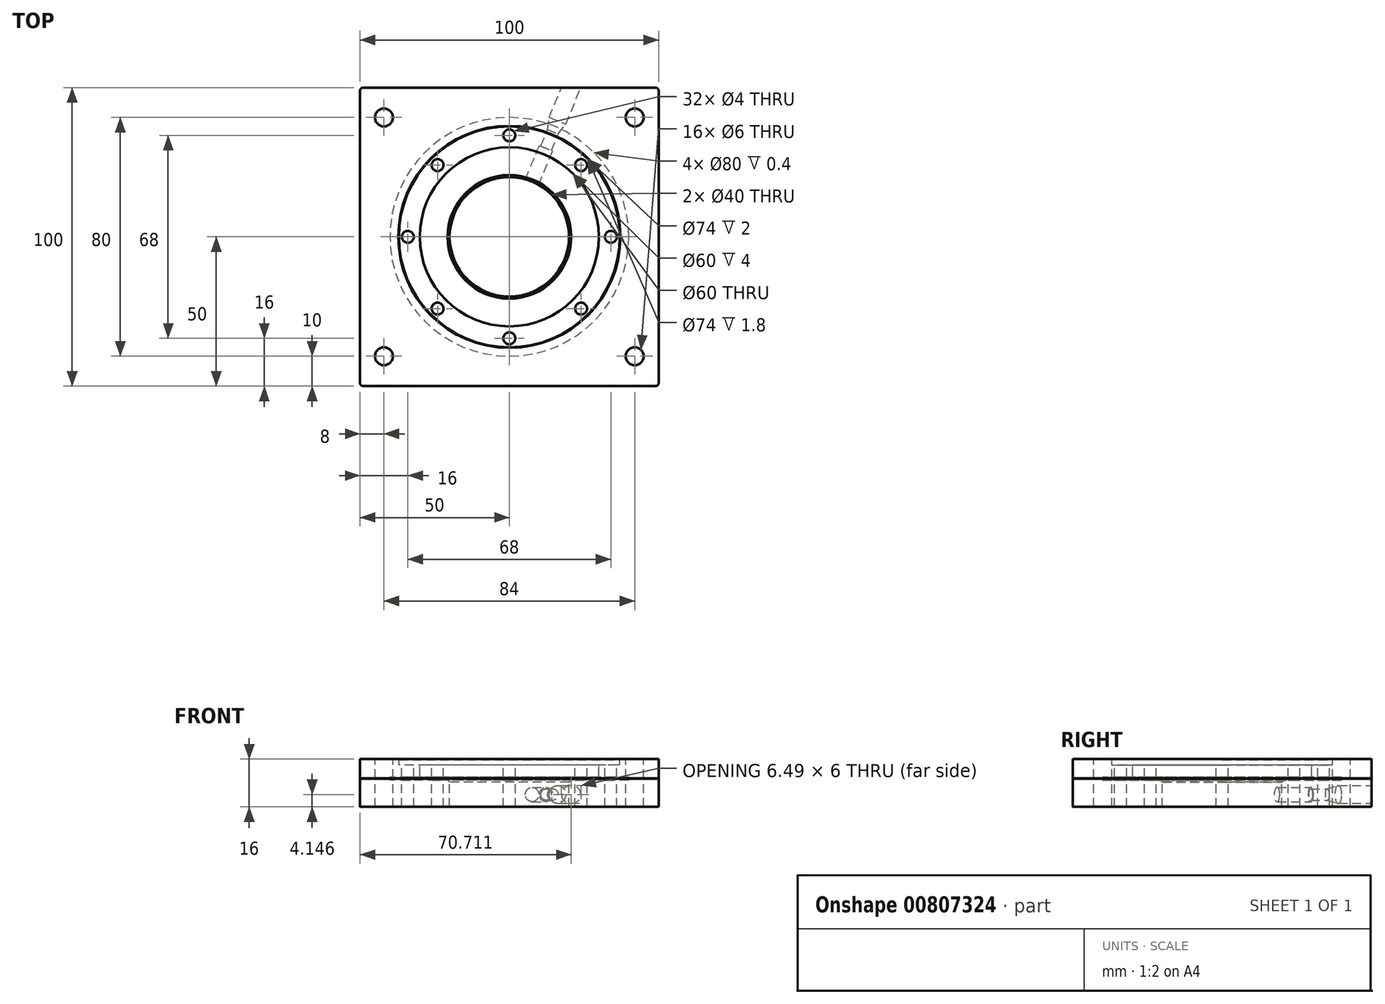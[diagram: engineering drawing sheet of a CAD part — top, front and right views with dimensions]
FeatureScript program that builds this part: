
annotation { "Feature Type Name" : "Feature", "Feature Type Description" : "" }
export const myFeature = defineFeature(function(context is Context, id is Id, definition is map)
    precondition{}
    {
        {
            var Q0;
            Q0=qCreatedBy(makeId("Front.planeOp"),FACE);
            var sketch = newSketch(context, id + "F0", { "sketchPlane" : qUnion([Q0])});
            skLineSegment(sketch, "E0", {"start": v(0, 61.42) * mm, "end": v(0, -61.42) * mm, "construction": true});
            skLineSegment(sketch, "E1", {"start": v(-106.58, 0) * mm, "end": v(106.58, 0) * mm, "construction": true});
            skPoint(sketch, "E2", {"position": v(0, 0) * mm});
            skLineSegment(sketch, "E3.bottom", {"start": v(-75, 8) * mm, "end": v(75, 8) * mm});
            skLineSegment(sketch, "E3.top", {"start": v(-75, -8) * mm, "end": v(75, -8) * mm});
            skLineSegment(sketch, "E3.left", {"start": v(-75, 8) * mm, "end": v(-75, -8) * mm});
            skLineSegment(sketch, "E3.right", {"start": v(75, 8) * mm, "end": v(75, -8) * mm});
            skLineSegment(sketch, "E4", {"start": v(-40, 2) * mm, "end": v(-40, 1) * mm});
            skLineSegment(sketch, "E5.MirrorCS", {"start": v(40, 2) * mm, "end": v(40, 1) * mm});
            skLineSegment(sketch, "E6", {"start": v(-37, 8) * mm, "end": v(-37, 6) * mm});
            skLineSegment(sketch, "E7", {"start": v(-20, 1) * mm, "end": v(-20, -8) * mm});
            skLineSegment(sketch, "E8.MirrorCS", {"start": v(20, 1) * mm, "end": v(20, -8) * mm});
            skLineSegment(sketch, "E9.MirrorCS", {"start": v(37, 8) * mm, "end": v(37, 6) * mm});
            skLineSegment(sketch, "E10", {"start": v(30, 6) * mm, "end": v(37, 6) * mm});
            skLineSegment(sketch, "E11", {"start": v(-40, 1) * mm, "end": v(40, 1) * mm});
            skLineSegment(sketch, "E12", {"start": v(-40, 1.6) * mm, "end": v(-75, 1.6) * mm});
            skLineSegment(sketch, "E13", {"start": v(-75, 1.4) * mm, "end": v(-40, 1.4) * mm});
            skLineSegment(sketch, "E14.MirrorCS", {"start": v(40, 1.6) * mm, "end": v(75, 1.6) * mm});
            skLineSegment(sketch, "E15.MirrorCS", {"start": v(75, 1.4) * mm, "end": v(40, 1.4) * mm});
            skLineSegment(sketch, "E16", {"start": v(-20, 0.3) * mm, "end": v(-20.7, 1) * mm});
            skLineSegment(sketch, "E17.MirrorCS", {"start": v(20, 0.3) * mm, "end": v(20.7, 1) * mm});
            skLineSegment(sketch, "E18", {"start": v(-20, 0.3) * mm, "end": v(20, 0.3) * mm});
            skPoint(sketch, "E19.newPointA", {"position": v(30, 6) * mm});
            skLineSegment(sketch, "E20", {"start": v(-30, 6) * mm, "end": v(-37, 6) * mm});
            skPoint(sketch, "E21.visualSharp", {"position": v(-30, 6) * mm});
            skLineSegment(sketch, "E22", {"start": v(-40, 2) * mm, "end": v(40, 2) * mm});
            skLineSegment(sketch, "E23", {"start": v(30, 6) * mm, "end": v(30, 2) * mm});
            skLineSegment(sketch, "E24", {"start": v(-30, 6) * mm, "end": v(-30, 2) * mm});
            skSolve(sketch);
        }
        {
            var Q0;
            {var subQ0=sQuery(id+"F0.wireOp",EDGE,"E6");Q0=makeQuery(id+"F0.imprint","IMPRINT",FACE,{"disambiguationData":[TD([[makeQuery(id+"F0.imprint","IMPRINT",EDGE,{"derivedFrom":subQ0}),-1.0]])]});}
            var Q1;
            {var subQ4=sQuery(id+"F0.wireOp",EDGE,"E13");Q1=makeQuery(id+"F0.imprint","IMPRINT",FACE,{"disambiguationData":[TD([[makeQuery(id+"F0.imprint","IMPRINT",EDGE,{"derivedFrom":subQ4}),-1.0]])]});}
            var Q2;
            {var subQ6=sQuery(id+"F0.wireOp",EDGE,"E15.MirrorCS");Q2=makeQuery(id+"F0.imprint","IMPRINT",FACE,{"disambiguationData":[TD([[makeQuery(id+"F0.imprint","IMPRINT",EDGE,{"derivedFrom":subQ6}),1.0]])]});}
            var Q3;
            {var subQ0=sQuery(id+"F0.wireOp",EDGE,"E9.MirrorCS");Q3=makeQuery(id+"F0.imprint","IMPRINT",FACE,{"disambiguationData":[TD([[makeQuery(id+"F0.imprint","IMPRINT",EDGE,{"derivedFrom":subQ0}),1.0]])]});}
            var Q4;
            Q4=sQuery(id+"F0.wireOp",EDGE,"E0");
            revolve(context, id + "F1", {"entities" : qUnion([Q0, Q1, Q2, Q3]), "axis" : qUnion([Q4]), "revolveType" : RevolveType.FULL});
        }
        {
            var Q0;
            {var subQ0=sQuery(id+"F0.wireOp",EDGE,"E3.bottom");Q0=makeQuery(id+"F1.opRevolve","SWEPT_FACE",FACE,{"disambiguationData":[OSD([subQ0]),TDD([makeQuery(id+"F0.imprint","IMPRINT",EDGE,{"disambiguationData":[TD([[makeQuery(id+"F0.imprint","INTERSECT",VERTEX,{"derivedFrom":[subQ0,sQuery(id+"F0.wireOp",EDGE,"E3.left")]}),-1.0]])],"derivedFrom":subQ0})])]});}
            var sketch = newSketch(context, id + "F2", { "sketchPlane" : qUnion([Q0])});
            skLineSegment(sketch, "E25.bottom", {"start": v(-50, 50) * mm, "end": v(50, 50) * mm});
            skLineSegment(sketch, "E25.top", {"start": v(-50, -50) * mm, "end": v(50, -50) * mm});
            skLineSegment(sketch, "E25.left", {"start": v(-50, 50) * mm, "end": v(-50, -50) * mm});
            skLineSegment(sketch, "E25.right", {"start": v(50, 50) * mm, "end": v(50, -50) * mm});
            skPoint(sketch, "E25.middle", {"position": v(0, 0) * mm});
            skLineSegment(sketch, "E26.bottom", {"start": v(-85, 85) * mm, "end": v(85, 85) * mm});
            skLineSegment(sketch, "E26.top", {"start": v(-85, -85) * mm, "end": v(85, -85) * mm});
            skLineSegment(sketch, "E26.left", {"start": v(-85, 85) * mm, "end": v(-85, -85) * mm});
            skLineSegment(sketch, "E26.right", {"start": v(85, 85) * mm, "end": v(85, -85) * mm});
            skSolve(sketch);
        }
        {
            var Q0;
            Q0=makeQuery(id+"F2.imprint","IMPRINT",FACE,{"disambiguationData":[TD([[makeQuery(id+"F2.imprint","IMPRINT",EDGE,{"derivedFrom":sQuery(id+"F2.wireOp",EDGE,"E26.bottom")}),-1.0]])]});
            var Q1;
            Q1=makeQuery(id+"F2.imprint","IMPRINT",FACE,{"disambiguationData":[TD([[makeQuery(id+"F2.imprint","IMPRINT",EDGE,{"derivedFrom":sQuery(id+"F2.wireOp",EDGE,"E25.bottom")}),1.0]])]});
            extrude(context, id + "F3", {"entities" : qUnion([Q0, Q1]), "operationType" : NewBodyOperationType.REMOVE, "endBound" : BoundingType.THROUGH_ALL, "oppositeDirection" : true, "depth" : 25 * mm, "offsetDistance" : 25 * mm});
        }
        {
            var Q0;
            {var subQ0=sQuery(id+"F0.wireOp",EDGE,"E3.bottom");Q0=makeQuery(id+"F1.opRevolve","SWEPT_FACE",FACE,{"disambiguationData":[OSD([subQ0]),TDD([makeQuery(id+"F0.imprint","IMPRINT",EDGE,{"disambiguationData":[TD([[makeQuery(id+"F0.imprint","INTERSECT",VERTEX,{"derivedFrom":[subQ0,sQuery(id+"F0.wireOp",EDGE,"E3.right")]}),1.0]])],"derivedFrom":subQ0})])]});}
            var sketch = newSketch(context, id + "F4", { "sketchPlane" : qUnion([Q0])});
            skLineSegment(sketch, "E27.0.0", {"start": v(-50, 50) * mm, "end": v(-50, -50) * mm});
            skLineSegment(sketch, "E27.0.1", {"start": v(-50, -50) * mm, "end": v(50, -50) * mm});
            skLineSegment(sketch, "E27.0.2", {"start": v(50, -50) * mm, "end": v(50, 50) * mm});
            skLineSegment(sketch, "E27.0.3", {"start": v(50, 50) * mm, "end": v(-50, 50) * mm});
            skCircle(sketch, "E28.0.0", {"center": v(0, 0) * mm, "radius": 37 * mm});
            skCircle(sketch, "E29.0", {"center": v(0, 0) * mm, "radius": 20 * mm});
            skCircle(sketch, "E30.0", {"center": v(0, 0) * mm, "radius": 20.7 * mm});
            skLineSegment(sketch, "E31", {"start": v(-50, 0) * mm, "end": v(50, 0) * mm, "construction": true});
            skLineSegment(sketch, "E32", {"start": v(0, 50) * mm, "end": v(0, -50) * mm, "construction": true});
            skLineSegment(sketch, "E33", {"start": v(-50, 40) * mm, "end": v(50, 40) * mm, "construction": true});
            skLineSegment(sketch, "E34", {"start": v(42, 50) * mm, "end": v(42, -50) * mm, "construction": true});
            skCircle(sketch, "E35", {"center": v(42, 40) * mm, "radius": 3 * mm});
            skCircle(sketch, "E36.0.1.0", {"center": v(42, -40) * mm, "radius": 3 * mm});
            skCircle(sketch, "E36.1.0.0", {"center": v(-42, 40) * mm, "radius": 3 * mm});
            skCircle(sketch, "E36.1.1.0", {"center": v(-42, -40) * mm, "radius": 3 * mm});
            skLineSegment(sketch, "E36.direction1", {"start": v(42, 40) * mm, "end": v(-42, 40) * mm, "construction": true});
            skLineSegment(sketch, "E36.direction2", {"start": v(42, 40) * mm, "end": v(42, -40) * mm, "construction": true});
            skCircle(sketch, "E37", {"center": v(0, 0) * mm, "radius": 34 * mm, "construction": true});
            skCircle(sketch, "E38.0", {"center": v(0, 0) * mm, "radius": 30 * mm});
            skCircle(sketch, "E39", {"center": v(0, 34) * mm, "radius": 2 * mm});
            skCircle(sketch, "E40.1.0", {"center": v(-24.04, 24.04) * mm, "radius": 2 * mm});
            skCircle(sketch, "E40.2.0", {"center": v(-34, 0) * mm, "radius": 2 * mm});
            skCircle(sketch, "E40.3.0", {"center": v(-24.04, -24.04) * mm, "radius": 2 * mm});
            skCircle(sketch, "E40.4.0", {"center": v(0, -34) * mm, "radius": 2 * mm});
            skCircle(sketch, "E40.5.0", {"center": v(24.04, -24.04) * mm, "radius": 2 * mm});
            skCircle(sketch, "E40.6.0", {"center": v(34, 0) * mm, "radius": 2 * mm});
            skCircle(sketch, "E40.7.0", {"center": v(24.04, 24.04) * mm, "radius": 2 * mm});
            skLineSegment(sketch, "E41", {"start": v(0, 0) * mm, "end": v(20.71, 50) * mm, "construction": true});
            skSolve(sketch);
        }
        {
            var Q0;
            Q0=makeQuery(id+"F4.imprint","IMPRINT",FACE,{"disambiguationData":[TD([[makeQuery(id+"F4.imprint","IMPRINT",EDGE,{"derivedFrom":sQuery(id+"F4.wireOp",EDGE,"E36.1.0.0")}),1.0]])]});
            var Q1;
            Q1=makeQuery(id+"F4.imprint","IMPRINT",FACE,{"disambiguationData":[TD([[makeQuery(id+"F4.imprint","IMPRINT",EDGE,{"derivedFrom":sQuery(id+"F4.wireOp",EDGE,"E35")}),1.0]])]});
            var Q2;
            Q2=makeQuery(id+"F4.imprint","IMPRINT",FACE,{"disambiguationData":[TD([[makeQuery(id+"F4.imprint","IMPRINT",EDGE,{"derivedFrom":sQuery(id+"F4.wireOp",EDGE,"E36.0.1.0")}),1.0]])]});
            var Q3;
            Q3=makeQuery(id+"F4.imprint","IMPRINT",FACE,{"disambiguationData":[TD([[makeQuery(id+"F4.imprint","IMPRINT",EDGE,{"derivedFrom":sQuery(id+"F4.wireOp",EDGE,"E36.1.1.0")}),1.0]])]});
            extrude(context, id + "F5", {"entities" : qUnion([Q0, Q1, Q2, Q3]), "operationType" : NewBodyOperationType.REMOVE, "endBound" : BoundingType.THROUGH_ALL, "oppositeDirection" : true, "depth" : 25 * mm, "offsetDistance" : 25 * mm});
        }
        {
            var Q0;
            Q0=makeQuery(id+"F4.imprint","IMPRINT",FACE,{"disambiguationData":[TD([[makeQuery(id+"F4.imprint","IMPRINT",EDGE,{"derivedFrom":sQuery(id+"F4.wireOp",EDGE,"E40.1.0")}),1.0]])]});
            var Q1;
            Q1=makeQuery(id+"F4.imprint","IMPRINT",FACE,{"disambiguationData":[TD([[makeQuery(id+"F4.imprint","IMPRINT",EDGE,{"derivedFrom":sQuery(id+"F4.wireOp",EDGE,"E39")}),1.0]])]});
            var Q2;
            Q2=makeQuery(id+"F4.imprint","IMPRINT",FACE,{"disambiguationData":[TD([[makeQuery(id+"F4.imprint","IMPRINT",EDGE,{"derivedFrom":sQuery(id+"F4.wireOp",EDGE,"E40.7.0")}),1.0]])]});
            var Q3;
            Q3=makeQuery(id+"F4.imprint","IMPRINT",FACE,{"disambiguationData":[TD([[makeQuery(id+"F4.imprint","IMPRINT",EDGE,{"derivedFrom":sQuery(id+"F4.wireOp",EDGE,"E40.6.0")}),1.0]])]});
            var Q4;
            Q4=makeQuery(id+"F4.imprint","IMPRINT",FACE,{"disambiguationData":[TD([[makeQuery(id+"F4.imprint","IMPRINT",EDGE,{"derivedFrom":sQuery(id+"F4.wireOp",EDGE,"E40.5.0")}),1.0]])]});
            var Q5;
            Q5=makeQuery(id+"F4.imprint","IMPRINT",FACE,{"disambiguationData":[TD([[makeQuery(id+"F4.imprint","IMPRINT",EDGE,{"derivedFrom":sQuery(id+"F4.wireOp",EDGE,"E40.4.0")}),1.0]])]});
            var Q6;
            Q6=makeQuery(id+"F4.imprint","IMPRINT",FACE,{"disambiguationData":[TD([[makeQuery(id+"F4.imprint","IMPRINT",EDGE,{"derivedFrom":sQuery(id+"F4.wireOp",EDGE,"E40.3.0")}),1.0]])]});
            var Q7;
            Q7=makeQuery(id+"F4.imprint","IMPRINT",FACE,{"disambiguationData":[TD([[makeQuery(id+"F4.imprint","IMPRINT",EDGE,{"derivedFrom":sQuery(id+"F4.wireOp",EDGE,"E40.2.0")}),1.0]])]});
            extrude(context, id + "F6", {"entities" : qUnion([Q0, Q1, Q2, Q3, Q4, Q5, Q6, Q7]), "operationType" : NewBodyOperationType.REMOVE, "endBound" : BoundingType.THROUGH_ALL, "oppositeDirection" : true, "depth" : 25 * mm, "offsetDistance" : 25 * mm});
        }
        {
            var Q0;
            {var subQ0=sQuery(id+"F0.wireOp",EDGE,"E3.top");Q0=makeQuery(id+"F1.opRevolve","SWEPT_FACE",FACE,{"disambiguationData":[OSD([subQ0]),TDD([makeQuery(id+"F0.imprint","IMPRINT",EDGE,{"disambiguationData":[TD([[makeQuery(id+"F0.imprint","INTERSECT",VERTEX,{"derivedFrom":[subQ0,sQuery(id+"F0.wireOp",EDGE,"E3.right")]}),1.0]])],"derivedFrom":subQ0})])]});}
            var sketch = newSketch(context, id + "F7", { "sketchPlane" : qUnion([Q0])});
            skLineSegment(sketch, "E42.0", {"start": v(-50, -50) * mm, "end": v(50, -50) * mm});
            skCircle(sketch, "E43.0", {"center": v(0, 0) * mm, "radius": 20 * mm, "construction": true});
            skLineSegment(sketch, "E44.0.0", {"start": v(50, 50) * mm, "end": v(-50, 50) * mm});
            skLineSegment(sketch, "E44.0.1", {"start": v(-50, 50) * mm, "end": v(-50, -50) * mm});
            skLineSegment(sketch, "E44.0.3", {"start": v(50, -50) * mm, "end": v(50, 50) * mm});
            skLineSegment(sketch, "E45.0", {"start": v(0, 0) * mm, "end": v(20.71, -50) * mm, "construction": true});
            skLineSegment(sketch, "E46.0", {"start": v(0, -50) * mm, "end": v(0, 50) * mm, "construction": true});
            skLineSegment(sketch, "E47.0", {"start": v(-50, 0) * mm, "end": v(50, 0) * mm, "construction": true});
            skSolve(sketch);
        }
        {
            var Q0;
            Q0=makeQuery(id+"F7.imprint","IMPRINT",FACE,{"disambiguationData":[TD([[makeQuery(id+"F7.imprint","IMPRINT",EDGE,{"derivedFrom":sQuery(id+"F7.wireOp",EDGE,"E44.0.0")}),-1.0]])]});
            cPlane(context, id + "F8", {"entities" : qUnion([Q0]), "cplaneType" : CPlaneType.OFFSET, "offset" : 4.15 * mm, "oppositeDirection" : true, "width" : 150 * mm, "height" : 150 * mm});
        }
        {
            var Q0;
            Q0=qCreatedBy(id+"F8.planeOp",FACE);
            var sketch = newSketch(context, id + "F9", { "sketchPlane" : qUnion([Q0])});
            skLineSegment(sketch, "E48.0", {"start": v(-50, -50) * mm, "end": v(50, -50) * mm});
            skLineSegment(sketch, "E49.0", {"start": v(50, -50) * mm, "end": v(50, 50) * mm});
            skLineSegment(sketch, "E50.0", {"start": v(-50, 50) * mm, "end": v(-50, -50) * mm});
            skLineSegment(sketch, "E51.0", {"start": v(50, 50) * mm, "end": v(-50, 50) * mm});
            skCircle(sketch, "E52.0", {"center": v(0, 0) * mm, "radius": 20 * mm, "construction": true});
            skLineSegment(sketch, "E53.0", {"start": v(0, -50) * mm, "end": v(0, 50) * mm, "construction": true});
            skLineSegment(sketch, "E54.0", {"start": v(-50, 0) * mm, "end": v(50, 0) * mm, "construction": true});
            skLineSegment(sketch, "E55.0", {"start": v(0, 0) * mm, "end": v(20.71, -50) * mm});
            skLineSegment(sketch, "E56", {"start": v(23.48, -48.85) * mm, "end": v(17.94, -51.15) * mm});
            skLineSegment(sketch, "E57", {"start": v(18.9, -37.77) * mm, "end": v(13.35, -40.06) * mm});
            skLineSegment(sketch, "E58", {"start": v(16.34, -34.5) * mm, "end": v(12.83, -35.95) * mm});
            skLineSegment(sketch, "E59", {"start": v(14.5, -28.76) * mm, "end": v(10.07, -30.6) * mm});
            skPoint(sketch, "E60", {"position": v(12.3, -29.67) * mm});
            skPoint(sketch, "E61", {"position": v(14.59, -35.22) * mm});
            skPoint(sketch, "E62", {"position": v(16.12, -38.91) * mm});
            skLineSegment(sketch, "E63", {"start": v(23.48, -48.85) * mm, "end": v(18.9, -37.77) * mm});
            skLineSegment(sketch, "E64", {"start": v(17.94, -51.15) * mm, "end": v(13.35, -40.06) * mm});
            skLineSegment(sketch, "E65", {"start": v(18.9, -37.77) * mm, "end": v(16.34, -34.5) * mm});
            skLineSegment(sketch, "E66", {"start": v(13.35, -40.06) * mm, "end": v(12.83, -35.95) * mm});
            skLineSegment(sketch, "E67", {"start": v(9.15, -15.82) * mm, "end": v(4.72, -17.66) * mm});
            skPoint(sketch, "E68", {"position": v(6.93, -16.74) * mm});
            skLineSegment(sketch, "E69", {"start": v(14.5, -28.76) * mm, "end": v(9.15, -15.82) * mm});
            skLineSegment(sketch, "E70", {"start": v(10.07, -30.6) * mm, "end": v(4.72, -17.66) * mm});
            skLineSegment(sketch, "E71", {"start": v(14.05, -28.95) * mm, "end": v(10.54, -30.4) * mm});
            skLineSegment(sketch, "E72", {"start": v(16.34, -34.5) * mm, "end": v(14.05, -28.95) * mm});
            skLineSegment(sketch, "E73", {"start": v(12.83, -35.95) * mm, "end": v(10.54, -30.4) * mm});
            skLineSegment(sketch, "E74", {"start": v(23.48, -48.85) * mm, "end": v(24.63, -51.62) * mm});
            skLineSegment(sketch, "E75", {"start": v(24.63, -51.62) * mm, "end": v(19.09, -53.92) * mm});
            skLineSegment(sketch, "E76", {"start": v(19.09, -53.92) * mm, "end": v(17.94, -51.15) * mm});
            skPoint(sketch, "E77", {"position": v(21.86, -52.77) * mm});
            skLineSegment(sketch, "E78", {"start": v(20.71, -50) * mm, "end": v(21.86, -52.77) * mm});
            skSolve(sketch);
        }
        {
            var Q0;
            {var subQ2=sQuery(id+"F9.wireOp",EDGE,"E76");Q0=makeQuery(id+"F9.imprint","IMPRINT",FACE,{"disambiguationData":[TD([[makeQuery(id+"F9.imprint","IMPRINT",EDGE,{"derivedFrom":subQ2}),-1.0]])]});}
            var Q1;
            {var subQ1=sQuery(id+"F9.wireOp",EDGE,"E48.0");var subQ3=sQuery(id+"F9.wireOp",EDGE,"E64");var subQ4=makeQuery(id+"F9.imprint","INTERSECT",VERTEX,{"derivedFrom":[subQ1,subQ3]});Q1=makeQuery(id+"F9.imprint","IMPRINT",FACE,{"disambiguationData":[TD([[makeQuery(id+"F9.imprint","IMPRINT",EDGE,{"disambiguationData":[TD([[subQ4,1.0]])],"derivedFrom":subQ3}),-1.0]])]});}
            var Q2;
            {var subQ0=sQuery(id+"F9.wireOp",EDGE,"E55.0");var subQ5=sQuery(id+"F9.wireOp",EDGE,"E57");var subQ7=makeQuery(id+"F9.imprint","INTERSECT",VERTEX,{"derivedFrom":[subQ0,subQ5]});Q2=makeQuery(id+"F9.imprint","IMPRINT",FACE,{"disambiguationData":[TD([[makeQuery(id+"F9.imprint","IMPRINT",EDGE,{"disambiguationData":[TD([[subQ7,-1.0]])],"derivedFrom":subQ5}),1.0]])]});}
            var Q3;
            {var subQ5=sQuery(id+"F9.wireOp",EDGE,"E66");Q3=makeQuery(id+"F9.imprint","IMPRINT",FACE,{"disambiguationData":[TD([[makeQuery(id+"F9.imprint","IMPRINT",EDGE,{"derivedFrom":subQ5}),-1.0]])]});}
            var Q4;
            {var subQ5=sQuery(id+"F9.wireOp",EDGE,"E73");Q4=makeQuery(id+"F9.imprint","IMPRINT",FACE,{"disambiguationData":[TD([[makeQuery(id+"F9.imprint","IMPRINT",EDGE,{"derivedFrom":subQ5}),-1.0]])]});}
            var Q5;
            {var subQ0=sQuery(id+"F9.wireOp",EDGE,"E70");Q5=makeQuery(id+"F9.imprint","IMPRINT",FACE,{"disambiguationData":[TD([[makeQuery(id+"F9.imprint","IMPRINT",EDGE,{"derivedFrom":subQ0}),-1.0]])]});}
            var Q6;
            Q6=sQuery(id+"F9.wireOp",EDGE,"E55.0");
            revolve(context, id + "F10", {"operationType" : NewBodyOperationType.REMOVE, "entities" : qUnion([Q0, Q1, Q2, Q3, Q4, Q5]), "axis" : qUnion([Q6]), "revolveType" : RevolveType.FULL, "oppositeDirection" : true});
        }
        {
            var Q0;
            Q0=makeQuery(id+"F1.opRevolve","SWEPT_EDGE",EDGE,{"disambiguationData":[OSD([sQuery(id+"F0.wireOp",EDGE,"E3.bottom"),sQuery(id+"F0.wireOp",EDGE,"E6")])]});
            chamfer(context, id + "F11", {"entities" : qUnion([Q0]), "width" : .2 * mm, "tangentPropagation" : true});
        }
        {
            var Q0;
            Q0=makeQuery(id+"F1.opRevolve","SWEPT_EDGE",EDGE,{"disambiguationData":[OSD([sQuery(id+"F0.wireOp",EDGE,"E20"),sQuery(id+"F0.wireOp",EDGE,"E24")])]});
            var Q1;
            Q1=makeQuery(id+"F1.opRevolve","SWEPT_EDGE",EDGE,{"disambiguationData":[OSD([sQuery(id+"F0.wireOp",EDGE,"E22"),sQuery(id+"F0.wireOp",EDGE,"E24")])]});
            fillet(context, id + "F12", {"entities" : qUnion([Q0, Q1]), "radius" : .4 * mm, "tangentPropagation" : true, "allowEdgeOverflow" : false});
        }
        {
            var Q0;
            {var subQ1=sQuery(id+"F2.wireOp",EDGE,"E25.left");var subQ2=sQuery(id+"F2.wireOp",EDGE,"E25.bottom");Q0=makeQuery(id+"F3.boolean.opBoolean","COPY",EDGE,{"disambiguationData":[TD([makeQuery(id+"F1.opRevolve","SWEPT_FACE",FACE,{"disambiguationData":[OSD([sQuery(id+"F0.wireOp",EDGE,"E13")])]})])],"derivedFrom":makeQuery(id+"F3.opExtrude","SWEPT_EDGE",EDGE,{"disambiguationData":[OSD([subQ2,subQ1])]})});}
            var Q1;
            {var subQ1=sQuery(id+"F2.wireOp",EDGE,"E25.bottom");var subQ2=sQuery(id+"F2.wireOp",EDGE,"E25.left");Q1=makeQuery(id+"F3.boolean.opBoolean","COPY",EDGE,{"disambiguationData":[TD([makeQuery(id+"F1.opRevolve","SWEPT_FACE",FACE,{"disambiguationData":[OSD([sQuery(id+"F0.wireOp",EDGE,"E12")])]})])],"derivedFrom":makeQuery(id+"F3.opExtrude","SWEPT_EDGE",EDGE,{"disambiguationData":[OSD([subQ1,subQ2])]})});}
            var Q2;
            {var subQ1=sQuery(id+"F2.wireOp",EDGE,"E25.top");var subQ2=sQuery(id+"F2.wireOp",EDGE,"E25.left");Q2=makeQuery(id+"F3.boolean.opBoolean","COPY",EDGE,{"disambiguationData":[TD([makeQuery(id+"F1.opRevolve","SWEPT_FACE",FACE,{"disambiguationData":[OSD([sQuery(id+"F0.wireOp",EDGE,"E12")])]})])],"derivedFrom":makeQuery(id+"F3.opExtrude","SWEPT_EDGE",EDGE,{"disambiguationData":[OSD([subQ1,subQ2])]})});}
            var Q3;
            {var subQ1=sQuery(id+"F2.wireOp",EDGE,"E25.left");var subQ2=sQuery(id+"F2.wireOp",EDGE,"E25.top");Q3=makeQuery(id+"F3.boolean.opBoolean","COPY",EDGE,{"disambiguationData":[TD([makeQuery(id+"F1.opRevolve","SWEPT_FACE",FACE,{"disambiguationData":[OSD([sQuery(id+"F0.wireOp",EDGE,"E13")])]})])],"derivedFrom":makeQuery(id+"F3.opExtrude","SWEPT_EDGE",EDGE,{"disambiguationData":[OSD([subQ2,subQ1])]})});}
            var Q4;
            {var subQ1=sQuery(id+"F2.wireOp",EDGE,"E25.top");var subQ2=sQuery(id+"F2.wireOp",EDGE,"E25.right");Q4=makeQuery(id+"F3.boolean.opBoolean","COPY",EDGE,{"disambiguationData":[TD([makeQuery(id+"F1.opRevolve","SWEPT_FACE",FACE,{"disambiguationData":[OSD([sQuery(id+"F0.wireOp",EDGE,"E13")])]})])],"derivedFrom":makeQuery(id+"F3.opExtrude","SWEPT_EDGE",EDGE,{"disambiguationData":[OSD([subQ1,subQ2])]})});}
            var Q5;
            {var subQ1=sQuery(id+"F2.wireOp",EDGE,"E25.top");var subQ2=sQuery(id+"F2.wireOp",EDGE,"E25.right");Q5=makeQuery(id+"F3.boolean.opBoolean","COPY",EDGE,{"disambiguationData":[TD([makeQuery(id+"F1.opRevolve","SWEPT_FACE",FACE,{"disambiguationData":[OSD([sQuery(id+"F0.wireOp",EDGE,"E12")])]})])],"derivedFrom":makeQuery(id+"F3.opExtrude","SWEPT_EDGE",EDGE,{"disambiguationData":[OSD([subQ1,subQ2])]})});}
            var Q6;
            {var subQ1=sQuery(id+"F2.wireOp",EDGE,"E25.bottom");var subQ2=sQuery(id+"F2.wireOp",EDGE,"E25.right");Q6=makeQuery(id+"F3.boolean.opBoolean","COPY",EDGE,{"disambiguationData":[TD([makeQuery(id+"F1.opRevolve","SWEPT_FACE",FACE,{"disambiguationData":[OSD([sQuery(id+"F0.wireOp",EDGE,"E12")])]})])],"derivedFrom":makeQuery(id+"F3.opExtrude","SWEPT_EDGE",EDGE,{"disambiguationData":[OSD([subQ1,subQ2])]})});}
            var Q7;
            {var subQ1=sQuery(id+"F2.wireOp",EDGE,"E25.bottom");var subQ2=sQuery(id+"F2.wireOp",EDGE,"E25.right");Q7=makeQuery(id+"F3.boolean.opBoolean","COPY",EDGE,{"disambiguationData":[TD([makeQuery(id+"F1.opRevolve","SWEPT_FACE",FACE,{"disambiguationData":[OSD([sQuery(id+"F0.wireOp",EDGE,"E13")])]})])],"derivedFrom":makeQuery(id+"F3.opExtrude","SWEPT_EDGE",EDGE,{"disambiguationData":[OSD([subQ1,subQ2])]})});}
            var Q8;
            {var subQ1=sQuery(id+"F2.wireOp",EDGE,"E25.top");var subQ2=sQuery(id+"F2.wireOp",EDGE,"E25.left");Q8=makeQuery(id+"F3.boolean.opBoolean","COPY",EDGE,{"disambiguationData":[TD([makeQuery(id+"F1.opRevolve","SWEPT_FACE",FACE,{"disambiguationData":[OSD([sQuery(id+"F0.wireOp",EDGE,"E14.MirrorCS")])]})])],"derivedFrom":makeQuery(id+"F3.opExtrude","SWEPT_EDGE",EDGE,{"disambiguationData":[OSD([subQ1,subQ2])]})});}
            var Q9;
            {var subQ1=sQuery(id+"F2.wireOp",EDGE,"E25.left");var subQ2=sQuery(id+"F2.wireOp",EDGE,"E25.top");Q9=makeQuery(id+"F3.boolean.opBoolean","COPY",EDGE,{"disambiguationData":[TD([makeQuery(id+"F1.opRevolve","SWEPT_FACE",FACE,{"disambiguationData":[OSD([sQuery(id+"F0.wireOp",EDGE,"E15.MirrorCS")])]})])],"derivedFrom":makeQuery(id+"F3.opExtrude","SWEPT_EDGE",EDGE,{"disambiguationData":[OSD([subQ2,subQ1])]})});}
            var Q10;
            {var subQ1=sQuery(id+"F2.wireOp",EDGE,"E25.top");var subQ2=sQuery(id+"F2.wireOp",EDGE,"E25.right");Q10=makeQuery(id+"F3.boolean.opBoolean","COPY",EDGE,{"disambiguationData":[TD([makeQuery(id+"F1.opRevolve","SWEPT_FACE",FACE,{"disambiguationData":[OSD([sQuery(id+"F0.wireOp",EDGE,"E14.MirrorCS")])]})])],"derivedFrom":makeQuery(id+"F3.opExtrude","SWEPT_EDGE",EDGE,{"disambiguationData":[OSD([subQ1,subQ2])]})});}
            var Q11;
            {var subQ1=sQuery(id+"F2.wireOp",EDGE,"E25.right");var subQ2=sQuery(id+"F2.wireOp",EDGE,"E25.top");Q11=makeQuery(id+"F3.boolean.opBoolean","COPY",EDGE,{"disambiguationData":[TD([makeQuery(id+"F1.opRevolve","SWEPT_FACE",FACE,{"disambiguationData":[OSD([sQuery(id+"F0.wireOp",EDGE,"E15.MirrorCS")])]})])],"derivedFrom":makeQuery(id+"F3.opExtrude","SWEPT_EDGE",EDGE,{"disambiguationData":[OSD([subQ2,subQ1])]})});}
            var Q12;
            {var subQ1=sQuery(id+"F2.wireOp",EDGE,"E25.bottom");var subQ2=sQuery(id+"F2.wireOp",EDGE,"E25.right");Q12=makeQuery(id+"F3.boolean.opBoolean","COPY",EDGE,{"disambiguationData":[TD([makeQuery(id+"F1.opRevolve","SWEPT_FACE",FACE,{"disambiguationData":[OSD([sQuery(id+"F0.wireOp",EDGE,"E14.MirrorCS")])]})])],"derivedFrom":makeQuery(id+"F3.opExtrude","SWEPT_EDGE",EDGE,{"disambiguationData":[OSD([subQ1,subQ2])]})});}
            var Q13;
            {var subQ1=sQuery(id+"F2.wireOp",EDGE,"E25.bottom");var subQ2=sQuery(id+"F2.wireOp",EDGE,"E25.right");Q13=makeQuery(id+"F3.boolean.opBoolean","COPY",EDGE,{"disambiguationData":[TD([makeQuery(id+"F1.opRevolve","SWEPT_FACE",FACE,{"disambiguationData":[OSD([sQuery(id+"F0.wireOp",EDGE,"E15.MirrorCS")])]})])],"derivedFrom":makeQuery(id+"F3.opExtrude","SWEPT_EDGE",EDGE,{"disambiguationData":[OSD([subQ1,subQ2])]})});}
            var Q14;
            {var subQ1=sQuery(id+"F2.wireOp",EDGE,"E25.bottom");var subQ2=sQuery(id+"F2.wireOp",EDGE,"E25.left");Q14=makeQuery(id+"F3.boolean.opBoolean","COPY",EDGE,{"disambiguationData":[TD([makeQuery(id+"F1.opRevolve","SWEPT_FACE",FACE,{"disambiguationData":[OSD([sQuery(id+"F0.wireOp",EDGE,"E14.MirrorCS")])]})])],"derivedFrom":makeQuery(id+"F3.opExtrude","SWEPT_EDGE",EDGE,{"disambiguationData":[OSD([subQ1,subQ2])]})});}
            var Q15;
            {var subQ1=sQuery(id+"F2.wireOp",EDGE,"E25.bottom");var subQ2=sQuery(id+"F2.wireOp",EDGE,"E25.left");Q15=makeQuery(id+"F3.boolean.opBoolean","COPY",EDGE,{"disambiguationData":[TD([makeQuery(id+"F1.opRevolve","SWEPT_FACE",FACE,{"disambiguationData":[OSD([sQuery(id+"F0.wireOp",EDGE,"E15.MirrorCS")])]})])],"derivedFrom":makeQuery(id+"F3.opExtrude","SWEPT_EDGE",EDGE,{"disambiguationData":[OSD([subQ1,subQ2])]})});}
            fillet(context, id + "F13", {"entities" : qUnion([Q0, Q1, Q2, Q3, Q4, Q5, Q6, Q7, Q8, Q9, Q10, Q11, Q12, Q13, Q14, Q15]), "radius" : 1 * mm, "tangentPropagation" : true, "allowEdgeOverflow" : false});
        }
    });
